# Revit family: Edelstahlrohrschelle f. Lüftungsrohre V2A, M 8, DN 63-112
name_source: partatom
category: HLS-Bauteile
revit_build: Autodesk Revit 2017 (Build: 20190507_1515(x64)
units: mm (PartAtom-declared; Revit-internal decimal feet)

## family parameters
Arbeitsebenenbasiert = Ja
Beim Laden mit Abzugskörper schneiden = Nein
Bemaßung runder Anschluss = Durchmesser verwenden
Gemeinsam genutzt = Ja
Immer vertikal = Nein
Raumberechnungspunkt = Nein
Teiletyp = Normal

## types (6) — shared parameters
A = 16 mm  [stored 0.0524934 ft]
Anschluss = M8
Anschlußhöhe = 16 mm
Bauart = zweiteilig
Baustoffklasse = B2
DF1 = 13 mm  [stored 0.0426509 ft]
DF2 = 28 mm  [stored 0.0918635 ft]
DS = 6 mm  [stored 0.019685 ft]
DVS = 6 mm  [stored 0.019685 ft]
Dämmstärke = 6 mm  [stored 0.019685 ft]
Fabrikat = MEFA
Farbe Schalldämmeinlage = schwarz
Firma = MEFA Befestigungs- und Montagesysteme GmbH
HGA = 8 mm  [stored 0.0262467 ft]
Kurztext1 = Lüftungsschelle Edelstahl V2A 20x2
MB = 20 mm  [stored 0.0656168 ft]
MD = 2 mm  [stored 0.00656168 ft]
Material = Edelstahl
Material Schalldämmeinlage = TPE
Materialmaße = 20x2 mm
Mengeneinheit = St
Rohraußendurchmesser Zoll = Zoll
Schalldämmeinlage = Gummi
Verschluss = Schraubenverschluss
Verschluss-Schraube = M6
Vorgabe-Ansicht = 1219 mm
max. Temperaturbeständigkeit = 100 °C
max. zul. Last horizontal = 0.00 kN
max. zul. Last vertikal = 0.00 kN
vpe = 50 St
zero-valued in all types: AB, Stärke Material, max. Rohraußendurchmesser, min. Rohraußendurchmesser

## per-type parameters (varying)
| type | Achsabstand | Artikelnummer | B | D | D0 | EAN | Gewicht | Gewicht pro Bauteil | H | Höhe | Kurztext2 | Nennweite DN Rohr | R | RM | Rohraußendurchmesser | S |
| Edelstahlrohrschelle f. Lüftungsrohre, M 8, DN 63 | 105 mm | 0468113 | 118 mm | 67 mm | 79 mm | 4250928411822 | 0.15 kg | 0.15 kg | 91 mm  [stored 0.298556 ft] | 91 mm | DN 63 M8 TPE | 63 mm  [stored 0.206693 ft] | 40 mm  [stored 0.131234 ft] | 42 mm | 66 mm  [stored 0.216535 ft] | 105 mm  [stored 0.344488 ft] |
| Edelstahlrohrschelle f. Lüftungsrohre, M 8, DN 71 | 113 mm | 0468114 | 126 mm | 75 mm | 87 mm  [stored 0.285433 ft] | 4250928411839 | 0.16 kg | 0.16 kg | 99 mm  [stored 0.324803 ft] | 99 mm | DN 71 M8 TPE | 71 mm  [stored 0.23294 ft] | 44 mm | 46 mm  [stored 0.150919 ft] | 74 mm  [stored 0.242782 ft] | 113 mm |
| Edelstahlrohrschelle f. Lüftungsrohre, M 8, DN 80 | 122 mm | 0468115 | 135 mm | 84 mm  [stored 0.275591 ft] | 96 mm  [stored 0.314961 ft] | 4250928411846 | 0.17 kg | 0.17 kg | 108 mm | 108 mm | DN 80 M8 TPE | 80 mm  [stored 0.262467 ft] | 48 mm  [stored 0.15748 ft] | 50 mm  [stored 0.164042 ft] | 83 mm  [stored 0.27231 ft] | 122 mm |
| Edelstahlrohrschelle f. Lüftungsrohre, M 8, DN 90 | 134 mm | 0468116 | 145 mm | 94 mm  [stored 0.308399 ft] | 106 mm  [stored 0.347769 ft] | 4250928411853 | 0.19 kg | 0.19 kg | 118 mm | 118 mm | DN 90 M8 TPE | 90 mm  [stored 0.295276 ft] | 53 mm  [stored 0.173885 ft] | 55 mm  [stored 0.180446 ft] | 93 mm  [stored 0.305118 ft] | 132 mm |
| Edelstahlrohrschelle f. Lüftungsrohre, M 8, DN100 | 143 mm | 0468117 | 156 mm | 105 mm  [stored 0.344488 ft] | 117 mm | 4250928411860 | 0.19 kg | 0.19 kg | 129 mm | 129 mm | DN 100 M8 TPE | 100 mm  [stored 0.328084 ft] | 59 mm | 61 mm | 104 mm | 143 mm |
| Edelstahlrohrschelle f. Lüftungsrohre, M 8, DN112 | 155 mm | 0468118 | 168 mm | 117 mm | 129 mm | 4250928411877 | 0.20 kg | 0.20 kg | 141 mm | 141 mm | DN 112 M8 TPE | 112 mm | 65 mm | 67 mm | 116 mm | 155 mm |

note: [stored X ft] marks values corroborated as IEEE doubles in the binary element streams (Revit-internal decimal feet)

## geometry (parser evidence)
native form markers: Sweep x7
no freeform markers — native parametric forms only
